# Revit family: AFX-Edge- LED_Flush_Mount
name_source: partatom
category: Lighting Fixtures
units: mm (PartAtom-declared; Revit-internal decimal feet)

## family parameters
Cut with Voids When Loaded = No
Host = Face
Light Source = Yes
Part Type = Normal
Room Calculation Point = No
Round Connector Dimension = Use Diameter
Shared = No

## types (2) — shared parameters
Apparent Load = 0 VA
Assembly Code = E2020200
Color Filter = 16777215
Colour Rendering Index = 90
Default Elevation = 48"
Depth = 15/16"
Diffuser Finish = AFX - Acrylic
Dimming Lamp Color Temperature Shift = <None>
Emit Shape Visible in Rendering = No
Emit from Circle Diameter = 13"
Housing Finish = AFX - Paint Finish Black
Keynote = 12500
Manufacturer = AFX Inc
Photometric Web File = EGRF1625LAJD1xx_IES.IES
Power Factor = 1
Product Documentation Link = https://www.afxinc.com
Revit Model Built By = https://www.servex-us.com
Sustainability = https://lamprecycle.org
Tilt Angle = 90.00°
Type Comments = Edge
URL = https://www.afxinc.com
Voltage = 120 V

## per-type parameters (varying)
| type | Description | Diameter | Wattage Comments |
| EGRF1625LAJD1BK | Led Flush Mount - 16" Dia x 15/16"D | 15 5/8" | 25w |
| EGRF2440LAJD1BK | Led Flush Mount - 24" Dia x 15/16"D | 23 5/8" | 40w |

note: column(s) folded — value = type name in every type: Model

## geometry (parser evidence)
native form markers: Sweep x2
no freeform markers — native parametric forms only
